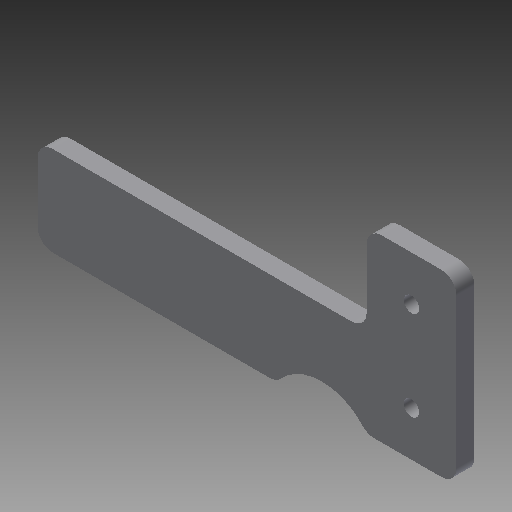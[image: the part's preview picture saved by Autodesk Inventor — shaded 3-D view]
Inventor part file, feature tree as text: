
AUTODESK INVENTOR PART (.ipt)
format: ipt  version: 2018 (Build 220112000, 112)  size: 109,056 bytes
history: native  units: mm
features: extrude x1, sketch x1
ambient origin geometry x8: Origin, YZ Plane, XZ Plane, XY Plane, X Axis, Y Axis, Z Axis, Center Point
bodies: Solid1 (feature_tree)
feature tree (2):
  extrude  "Extrusion1"  Depth=5.0mm
  sketch  "Sketch1"  dims[d5=5.0mm d6=5.0mm d8=5.0mm d9=5.0mm d10=5.0mm d11=5.0mm d12=5.0mm d14=60.0mm d18=5.2mm d19=5.2mm d20=6.0mm d21=0.0mm]
